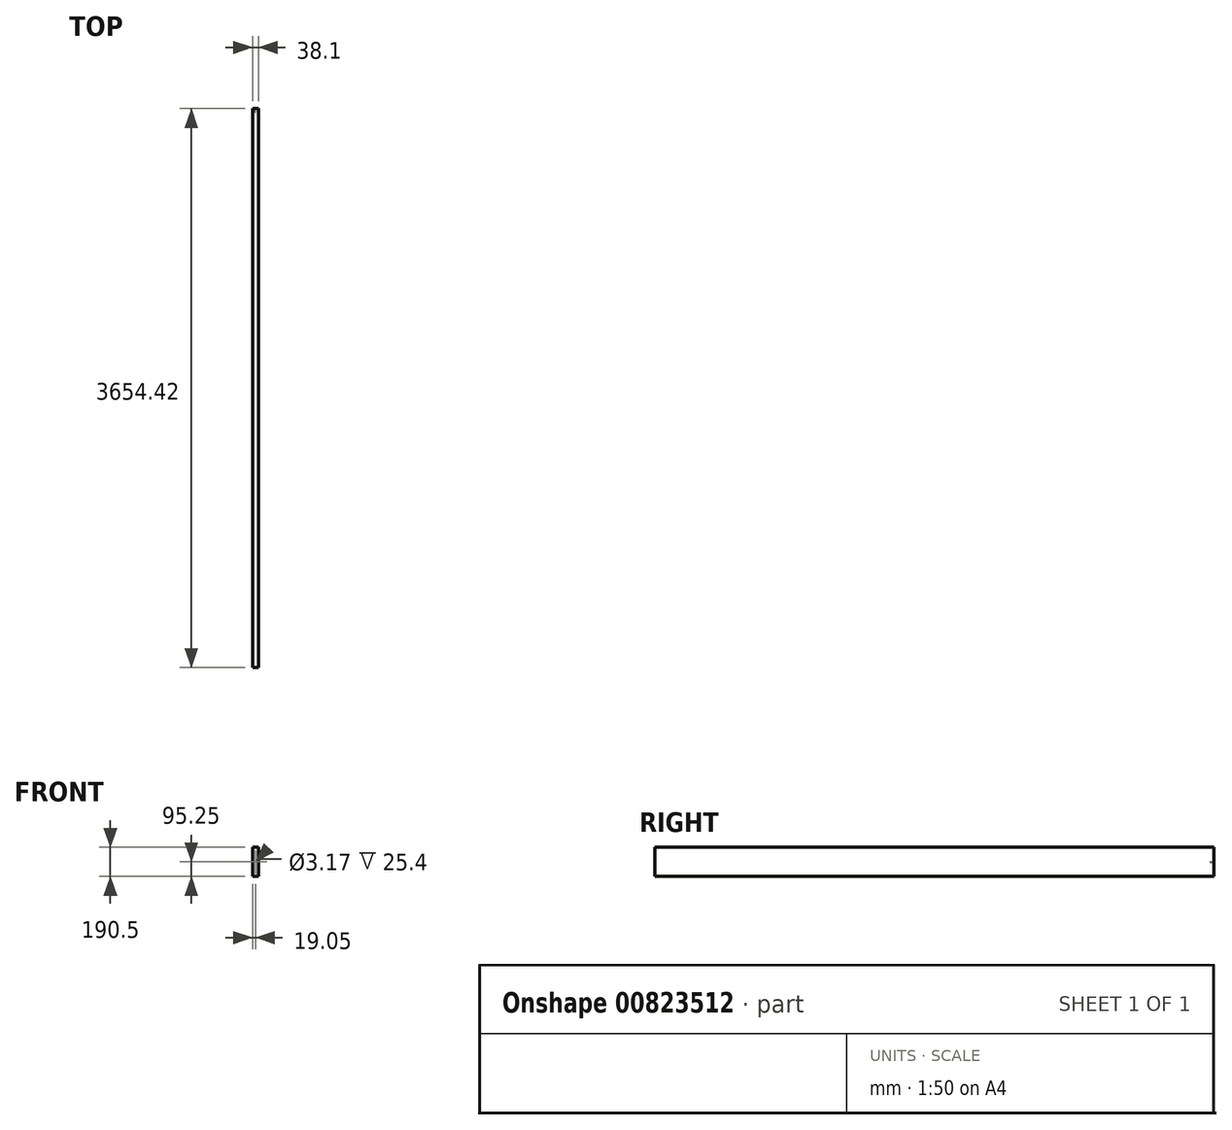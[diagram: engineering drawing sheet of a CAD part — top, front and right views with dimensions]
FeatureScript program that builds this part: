
annotation { "Feature Type Name" : "Feature", "Feature Type Description" : "" }
export const myFeature = defineFeature(function(context is Context, id is Id, definition is map)
    precondition{}
    {
        {
            var Q0;
            Q0=qCreatedBy(makeId("Front.planeOp"),FACE);
            var sketch = newSketch(context, id + "F0", { "sketchPlane" : qUnion([Q0])});
            skLineSegment(sketch, "E0.bottom", {"start": v(-19.05, -95.25) * mm, "end": v(19.05, -95.25) * mm});
            skLineSegment(sketch, "E0.top", {"start": v(-19.05, 95.25) * mm, "end": v(19.05, 95.25) * mm});
            skLineSegment(sketch, "E0.left", {"start": v(-19.05, -95.25) * mm, "end": v(-19.05, 95.25) * mm});
            skLineSegment(sketch, "E0.right", {"start": v(19.05, -95.25) * mm, "end": v(19.05, 95.25) * mm});
            skSolve(sketch);
        }
        {
            var Q0;
            Q0=qSketchRegion(id+"F0",true);
            extrude(context, id + "F1", {"entities" : qUnion([Q0]), "depth" : 3654.42 * mm, "offsetDistance" : 25.4 * mm});
        }
        {
            var Q0;
            Q0=makeQuery(id+"F1.opExtrude","CAP_FACE",FACE,{"disambiguationData":[OSD([sQuery(id+"F0.wireOp",EDGE,"E0.bottom"),sQuery(id+"F0.wireOp",EDGE,"E0.top"),sQuery(id+"F0.wireOp",EDGE,"E0.left"),sQuery(id+"F0.wireOp",EDGE,"E0.right")])],"isStart":true});
            var sketch = newSketch(context, id + "F2", { "sketchPlane" : qUnion([Q0])});
            skCircle(sketch, "E1", {"center": v(0, 0) * mm, "radius": 1.59 * mm});
            skSolve(sketch);
        }
        {
            var Q0;
            Q0 = qSketchRegion(id + "F2", true);
            extrude(context, id + "F3", {"entities" : qUnion([Q0]), "operationType" : NewBodyOperationType.REMOVE, "oppositeDirection" : true, "depth" : 25.4 * mm, "offsetDistance" : 25.4 * mm});
        }
    });
